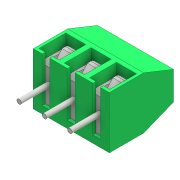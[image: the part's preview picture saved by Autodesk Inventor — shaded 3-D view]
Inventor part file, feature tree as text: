
AUTODESK INVENTOR PART (.ipt)
format: ipt  version: 2016 (Build 200138000, 138)  size: 270,848 bytes
history: native  units: mm
features: other x10, sketch x3
ambient origin geometry x8: Origin, YZ Plane, XZ Plane, XY Plane, X Axis, Y Axis, Z Axis, Center Point
bodies: Solid1 (feature_tree), Solid2 (feature_tree), Solid3 (feature_tree), Solid4 (feature_tree), Solid5 (feature_tree), Solid6 (feature_tree), Solid7 (feature_tree), Solid8 (feature_tree), Solid9 (feature_tree), Solid10 (feature_tree)
feature tree (13):
  sketch  "Sketch1"
  sketch  "Sketch2"
  sketch  "Sketch3"
  other  "Enlèv. mat.-Extru.3"
  other  "Boss.-Extru.4"
  other  "Extru.-Mince1"
  other  "Répétition linéaire2"
  other  "Répétition linéaire3[1]"
  other  "Répétition linéaire3[2]"
  other  "Répétition linéaire3[3]"
  other  "Répétition linéaire3[4]"
  other  "Répétition linéaire3[5]"
  other  "Répétition linéaire3[6]"
